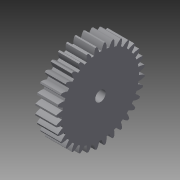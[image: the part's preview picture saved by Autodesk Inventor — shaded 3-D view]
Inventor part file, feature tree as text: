
AUTODESK INVENTOR PART (.ipt)
format: ipt  version: 2015 (Build 190159000, 159)  size: 318,976 bytes
history: native  units: in
note: dims shown in document units (in); Inventor stores cm internally (conversion verified against a paired STEP export)
features: other x1, extrude x1, imported_body x1, sketch x1
ambient origin geometry x8: Origin, YZ Plane, XZ Plane, XY Plane, X Axis, Y Axis, Z Axis, Center Point
bodies: Solid1 (feature_tree)
feature tree (4):
  other  "User Library-615290 32t Hitec pinion gear.sat1"
  extrude  "Extrusion1"  Depth=12.5984in TaperAngle=360.0deg
  imported_body  "Base1"
  sketch  "Sketch1"  dims[d0=0.2in d1=12.5984in d3=360.0deg d5=1.0in d6=0.0in]
